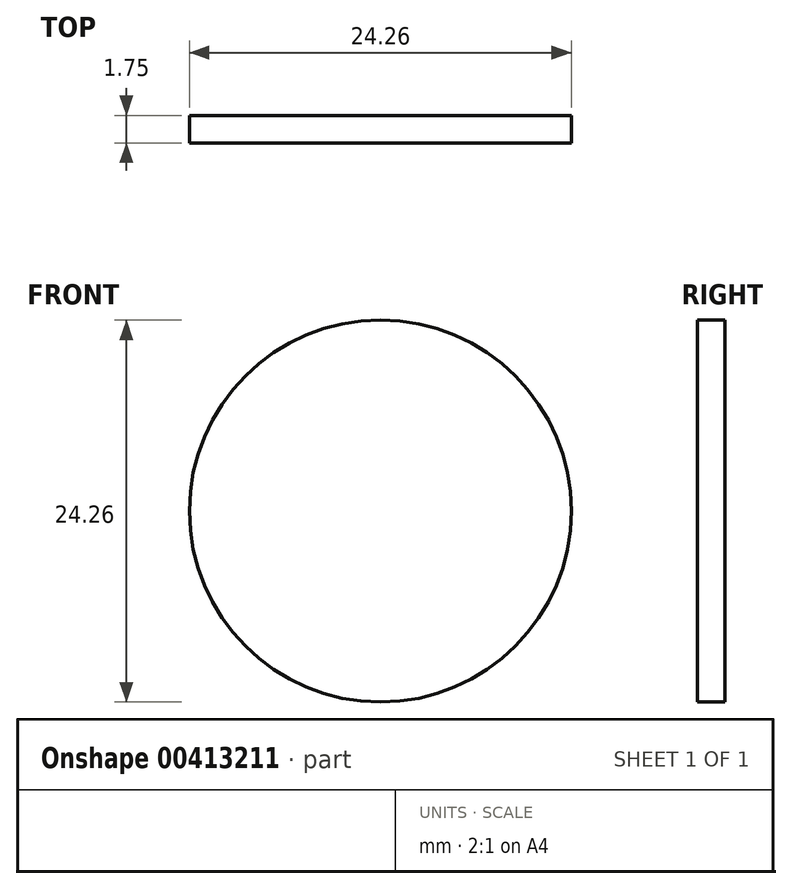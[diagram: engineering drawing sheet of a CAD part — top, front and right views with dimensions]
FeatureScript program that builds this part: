
annotation { "Feature Type Name" : "Feature", "Feature Type Description" : "" }
export const myFeature = defineFeature(function(context is Context, id is Id, definition is map)
    precondition{}
    {
        {
            var Q0;
            Q0=qCreatedBy(makeId("Front.planeOp"),FACE);
            var sketch = newSketch(context, id + "F0", { "sketchPlane" : qUnion([Q0])});
            skCircle(sketch, "E0", {"center": v(0, 0) * mm, "radius": 12.13 * mm});
            skSolve(sketch);
        }
        {
            var Q0;
            Q0=makeQuery(id+"F0.imprint","IMPRINT",FACE,{"disambiguationData":[TD([[makeQuery(id+"F0.imprint","IMPRINT",EDGE,{"derivedFrom":sQuery(id+"F0.wireOp",EDGE,"E0")}),1.0]])]});
            extrude(context, id + "F1", {"entities" : qUnion([Q0]), "depth" : 1.75 * mm});
        }
    });
